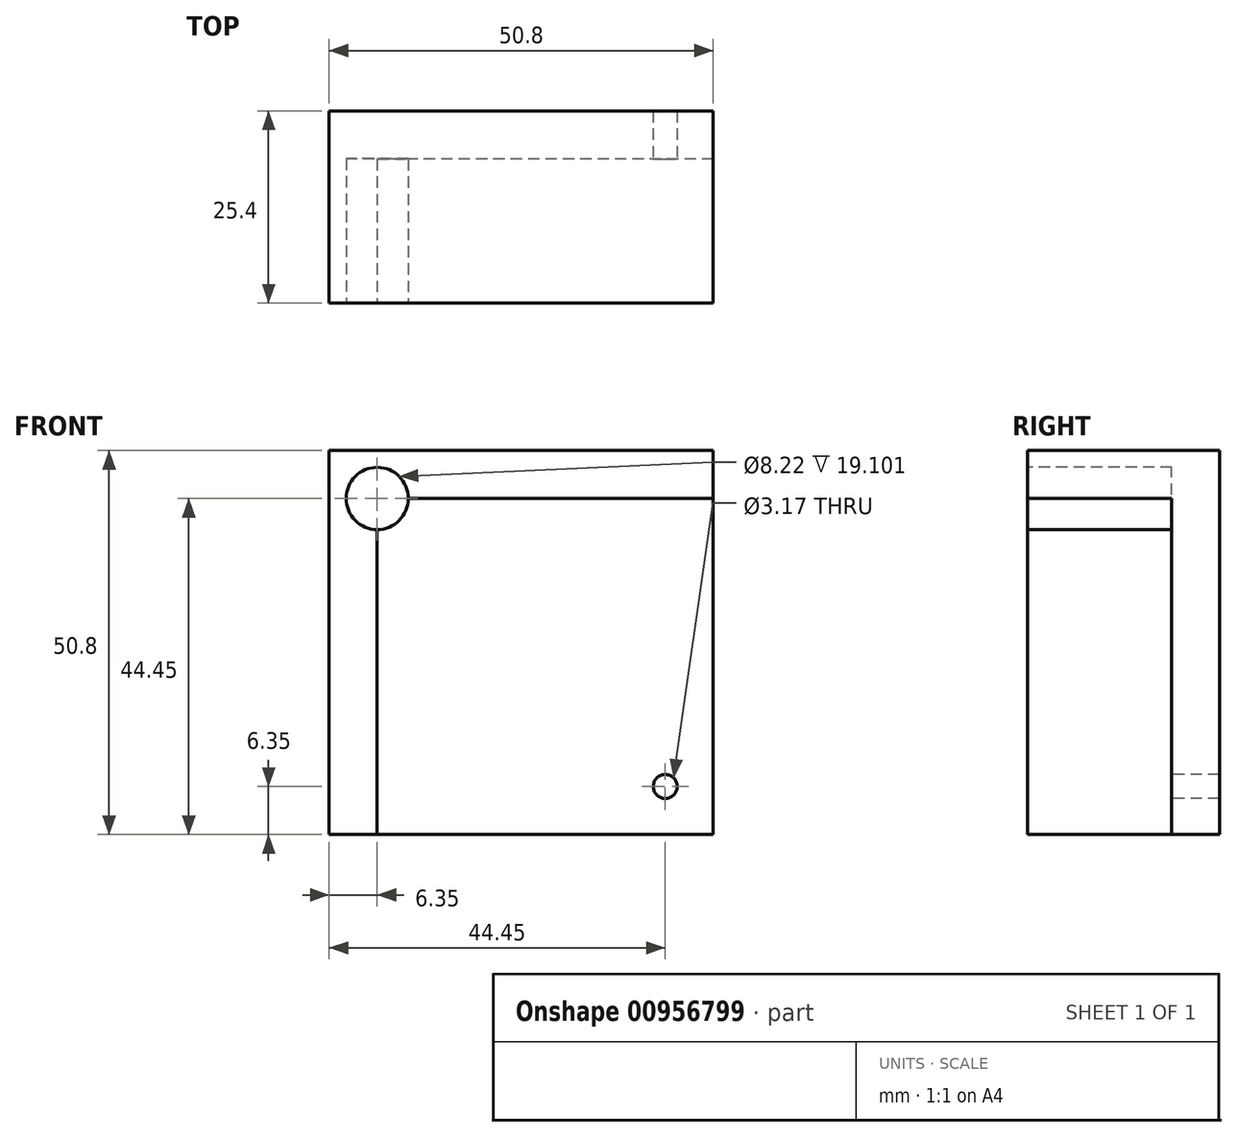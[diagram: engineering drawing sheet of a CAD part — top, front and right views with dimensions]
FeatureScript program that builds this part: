
annotation { "Feature Type Name" : "Feature", "Feature Type Description" : "" }
export const myFeature = defineFeature(function(context is Context, id is Id, definition is map)
    precondition{}
    {
        {
            var Q0;
            Q0=qCreatedBy(makeId("Front.planeOp"),FACE);
            var sketch = newSketch(context, id + "F0", { "sketchPlane" : qUnion([Q0])});
            skLineSegment(sketch, "E0.bottom", {"start": v(25.4, -25.4) * mm, "end": v(-25.4, -25.4) * mm});
            skLineSegment(sketch, "E0.top", {"start": v(25.4, 25.4) * mm, "end": v(-25.4, 25.4) * mm});
            skLineSegment(sketch, "E0.left", {"start": v(25.4, -25.4) * mm, "end": v(25.4, 25.4) * mm});
            skLineSegment(sketch, "E0.right", {"start": v(-25.4, -25.4) * mm, "end": v(-25.4, 25.4) * mm});
            skPoint(sketch, "E0.middle", {"position": v(0, 0) * mm});
            skSolve(sketch);
        }
        {
            var Q0;
            Q0 = qSketchRegion(id + "F0", true);
            extrude(context, id + "F1", {"entities" : qUnion([Q0]), "depth" : 25.4 * mm, "offsetDistance" : 25.4 * mm});
        }
        {
            var Q0;
            Q0=makeQuery(id+"F1.opExtrude","CAP_FACE",FACE,{"disambiguationData":[OSD([sQuery(id+"F0.wireOp",EDGE,"E0.bottom"),sQuery(id+"F0.wireOp",EDGE,"E0.top"),sQuery(id+"F0.wireOp",EDGE,"E0.left"),sQuery(id+"F0.wireOp",EDGE,"E0.right")])],"isStart":false});
            var sketch = newSketch(context, id + "F2", { "sketchPlane" : qUnion([Q0])});
            skLineSegment(sketch, "E1.bottom", {"start": v(25.4, -25.4) * mm, "end": v(-19.05, -25.4) * mm});
            skLineSegment(sketch, "E1.top", {"start": v(25.4, 19.05) * mm, "end": v(-19.05, 19.05) * mm});
            skLineSegment(sketch, "E1.left", {"start": v(25.4, -25.4) * mm, "end": v(25.4, 19.05) * mm});
            skLineSegment(sketch, "E1.right", {"start": v(-19.05, -25.4) * mm, "end": v(-19.05, 19.05) * mm});
            skSolve(sketch);
        }
        {
            var Q0;
            Q0 = qSketchRegion(id + "F2", true);
            extrude(context, id + "F3", {"entities" : qUnion([Q0]), "operationType" : NewBodyOperationType.REMOVE, "oppositeDirection" : true, "depth" : 19.05 * mm, "offsetDistance" : 25.4 * mm});
        }
        {
            var Q0;
            Q0=makeQuery(id+"F3.boolean.opBoolean","COPY",FACE,{"derivedFrom":makeQuery(id+"F3.opExtrude","CAP_FACE",FACE,{"disambiguationData":[OSD([sQuery(id+"F2.wireOp",EDGE,"E1.bottom"),sQuery(id+"F2.wireOp",EDGE,"E1.top"),sQuery(id+"F2.wireOp",EDGE,"E1.left"),sQuery(id+"F2.wireOp",EDGE,"E1.right")])],"isStart":false})});
            var sketch = newSketch(context, id + "F4", { "sketchPlane" : qUnion([Q0])});
            skCircle(sketch, "E2", {"center": v(19.05, -19.05) * mm, "radius": 1.59 * mm});
            skSolve(sketch);
        }
        {
            var Q0;
            Q0=makeQuery(id+"F1.opExtrude","CAP_FACE",FACE,{"disambiguationData":[OSD([sQuery(id+"F0.wireOp",EDGE,"E0.bottom"),sQuery(id+"F0.wireOp",EDGE,"E0.top"),sQuery(id+"F0.wireOp",EDGE,"E0.left"),sQuery(id+"F0.wireOp",EDGE,"E0.right")])],"isStart":false});
            var sketch = newSketch(context, id + "F5", { "sketchPlane" : qUnion([Q0])});
            skCircle(sketch, "E3", {"center": v(-19.05, 19.05) * mm, "radius": 4.11 * mm});
            skSolve(sketch);
        }
        {
            var Q0;
            Q0 = qSketchRegion(id + "F5", true);
            extrude(context, id + "F6", {"entities" : qUnion([Q0]), "operationType" : NewBodyOperationType.REMOVE, "oppositeDirection" : true, "depth" : 19.1 * mm, "offsetDistance" : 25.4 * mm});
        }
        {
            var Q0;
            Q0 = qSketchRegion(id + "F4", true);
            extrude(context, id + "F7", {"entities" : qUnion([Q0]), "operationType" : NewBodyOperationType.REMOVE, "oppositeDirection" : true, "depth" : 6.35 * mm, "offsetDistance" : 25.4 * mm});
        }
    });
